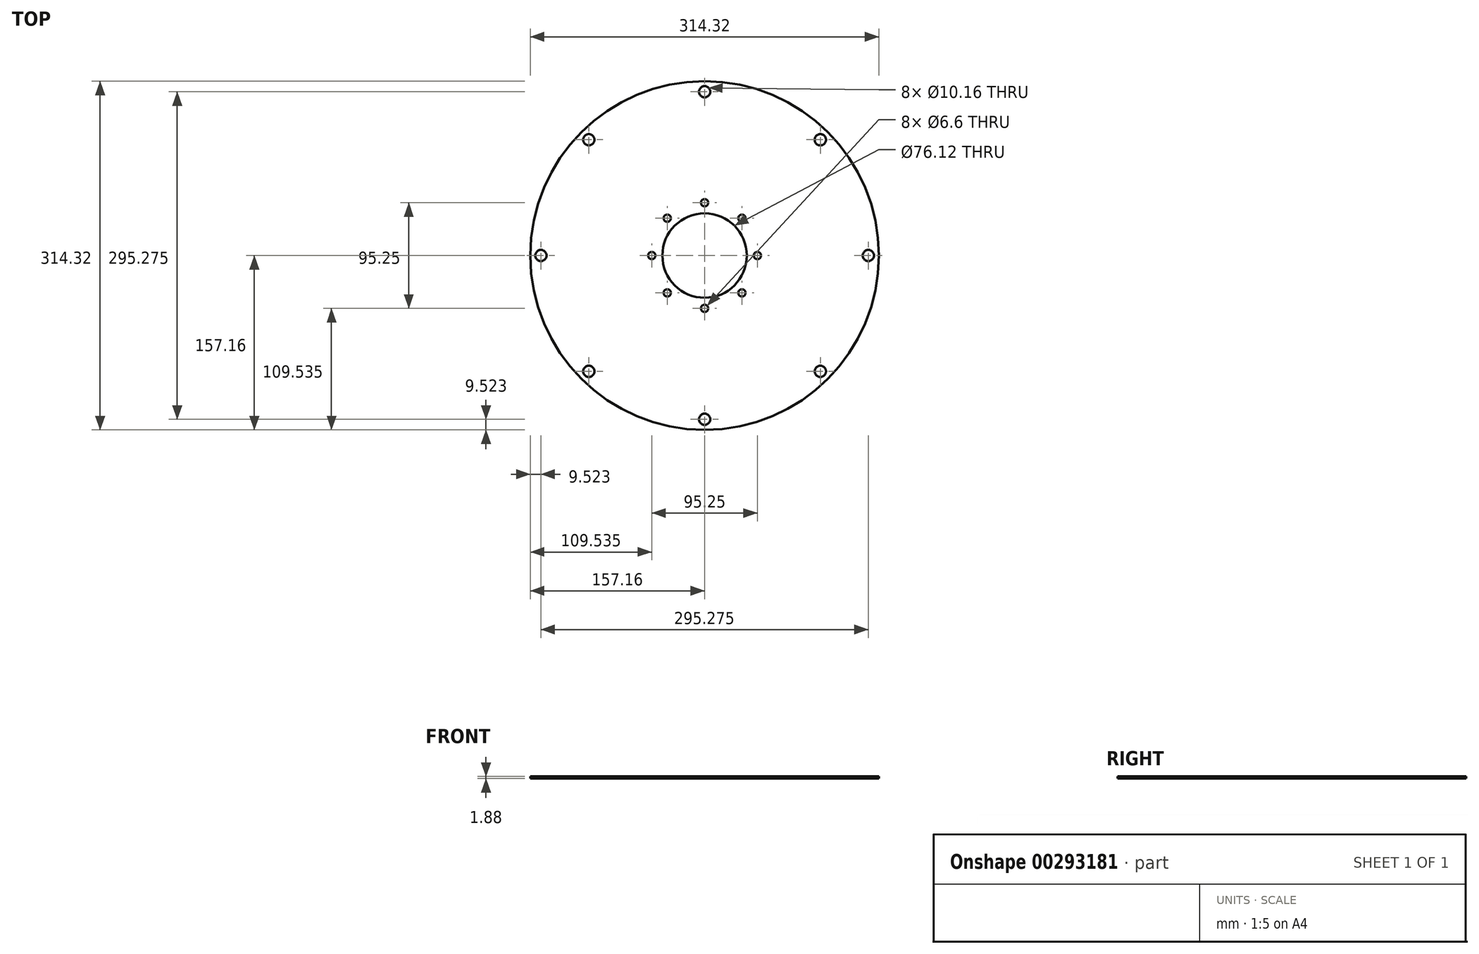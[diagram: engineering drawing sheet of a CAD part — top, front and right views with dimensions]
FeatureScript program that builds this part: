
annotation { "Feature Type Name" : "Feature", "Feature Type Description" : "" }
export const myFeature = defineFeature(function(context is Context, id is Id, definition is map)
    precondition{}
    {
        {
            var Q0;
            Q0=qCreatedBy(makeId("Top.planeOp"),FACE);
            var sketch = newSketch(context, id + "F0", { "sketchPlane" : qUnion([Q0])});
            skCircle(sketch, "E0", {"center": v(0, 0) * mm, "radius": 157.16 * mm});
            skCircle(sketch, "E1", {"center": v(0, 0) * mm, "radius": 38.06 * mm});
            skCircle(sketch, "E2", {"center": v(0, 147.64) * mm, "radius": 5.08 * mm});
            skCircle(sketch, "E3", {"center": v(0, 47.63) * mm, "radius": 3.3 * mm});
            skCircle(sketch, "E4.1.0", {"center": v(-104.4, 104.4) * mm, "radius": 5.08 * mm});
            skCircle(sketch, "E4.2.0", {"center": v(-147.64, 0) * mm, "radius": 5.08 * mm});
            skCircle(sketch, "E4.3.0", {"center": v(-104.4, -104.4) * mm, "radius": 5.08 * mm});
            skCircle(sketch, "E4.4.0", {"center": v(0, -147.64) * mm, "radius": 5.08 * mm});
            skCircle(sketch, "E4.5.0", {"center": v(104.4, -104.4) * mm, "radius": 5.08 * mm});
            skCircle(sketch, "E4.6.0", {"center": v(147.64, 0) * mm, "radius": 5.08 * mm});
            skCircle(sketch, "E4.7.0", {"center": v(104.4, 104.4) * mm, "radius": 5.08 * mm});
            skCircle(sketch, "E5.1.0", {"center": v(-33.68, 33.68) * mm, "radius": 3.3 * mm});
            skCircle(sketch, "E5.2.0", {"center": v(-47.63, 0) * mm, "radius": 3.3 * mm});
            skCircle(sketch, "E5.3.0", {"center": v(-33.68, -33.68) * mm, "radius": 3.3 * mm});
            skCircle(sketch, "E5.4.0", {"center": v(0, -47.63) * mm, "radius": 3.3 * mm});
            skCircle(sketch, "E5.5.0", {"center": v(33.68, -33.68) * mm, "radius": 3.3 * mm});
            skCircle(sketch, "E5.6.0", {"center": v(47.63, 0) * mm, "radius": 3.3 * mm});
            skCircle(sketch, "E5.7.0", {"center": v(33.68, 33.68) * mm, "radius": 3.3 * mm});
            skSolve(sketch);
        }
        {
            var Q0;
            Q0=makeQuery(id+"F0.imprint","IMPRINT",FACE,{"disambiguationData":[TD([[makeQuery(id+"F0.imprint","IMPRINT",EDGE,{"derivedFrom":sQuery(id+"F0.wireOp",EDGE,"E0")}),1.0]])]});
            extrude(context, id + "F1", {"entities" : qUnion([Q0]), "depth" : 1.88 * mm});
        }
    });
